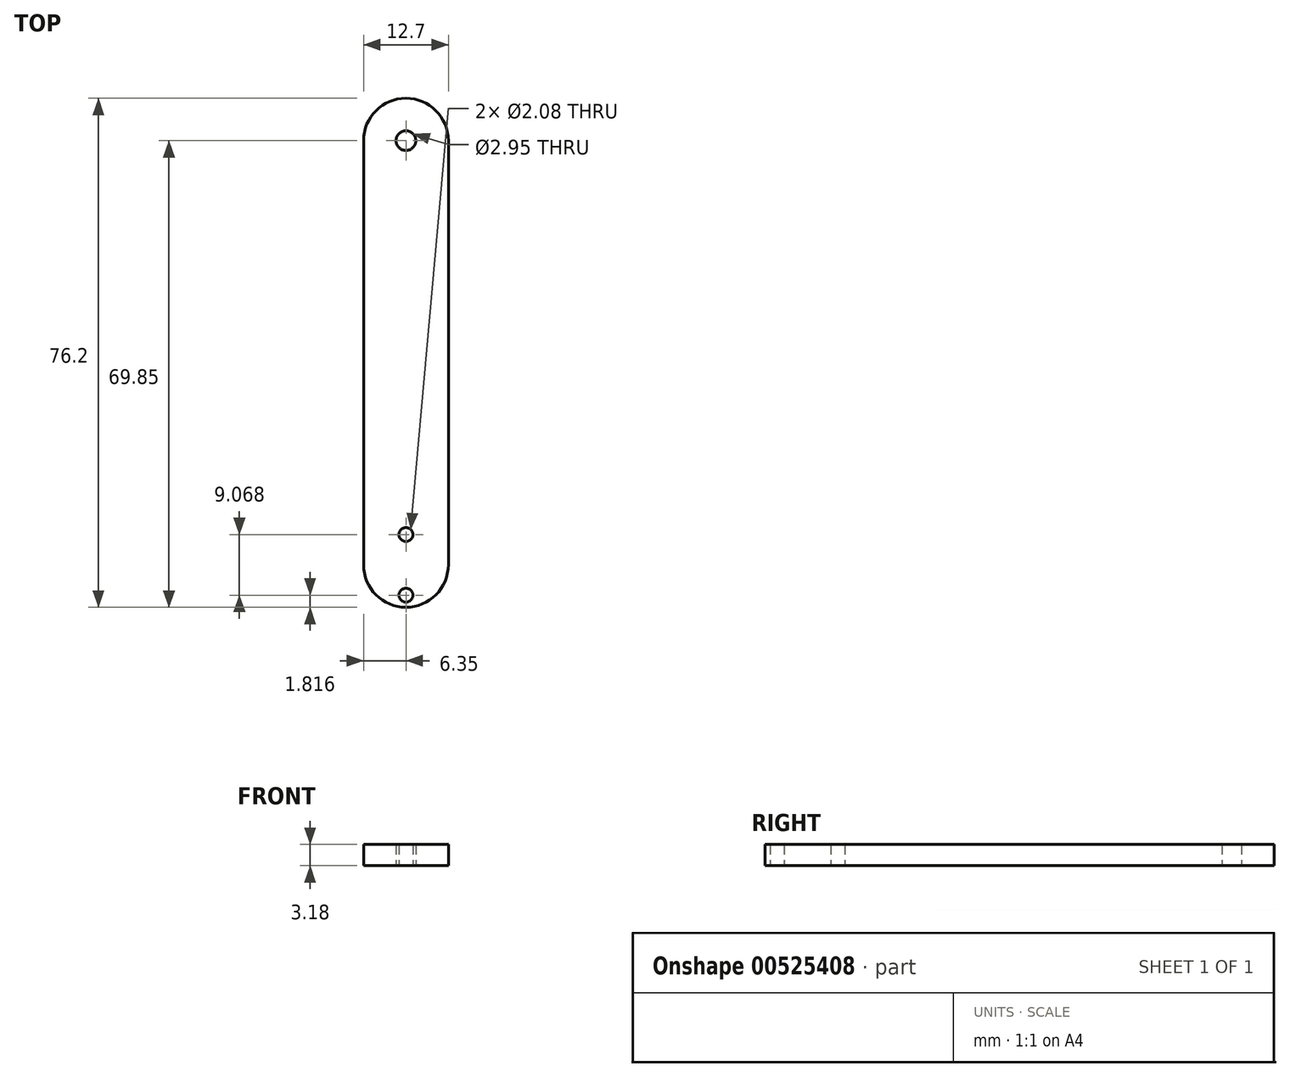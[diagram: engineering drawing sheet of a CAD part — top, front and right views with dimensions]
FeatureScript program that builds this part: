
annotation { "Feature Type Name" : "Feature", "Feature Type Description" : "" }
export const myFeature = defineFeature(function(context is Context, id is Id, definition is map)
    precondition{}
    {
        {
            var Q0;
            Q0=qCreatedBy(makeId("Top.planeOp"),FACE);
            var sketch = newSketch(context, id + "F0", { "sketchPlane" : qUnion([Q0])});
            skLineSegment(sketch, "E0.bottom", {"start": v(0, 38.1) * mm, "end": v(0, 38.1) * mm});
            skLineSegment(sketch, "E0.top", {"start": v(0, -38.1) * mm, "end": v(0, -38.1) * mm});
            skLineSegment(sketch, "E0.left", {"start": v(6.35, 31.75) * mm, "end": v(6.35, -31.75) * mm});
            skLineSegment(sketch, "E0.right", {"start": v(-6.35, 31.75) * mm, "end": v(-6.35, -31.75) * mm});
            skPoint(sketch, "E0.middle", {"position": v(0, 0) * mm});
            skCircle(sketch, "E1", {"center": v(0, -31.75) * mm, "radius": 1.47 * mm, "construction": true});
            skCircle(sketch, "E2.MirrorC", {"center": v(0, 31.75) * mm, "radius": 1.47 * mm});
            skPoint(sketch, "E3.visualSharp", {"position": v(6.35, 38.1) * mm});
            skArc(sketch, "E3.filletArc", {"start": v(6.35, 31.75) * mm, "mid": v(4.5, 36.24) * mm, "end": v(0, 38.1) * mm});
            skPoint(sketch, "E4.visualSharp", {"position": v(-6.35, 38.1) * mm});
            skArc(sketch, "E4.filletArc", {"start": v(0, 38.1) * mm, "mid": v(-4.5, 36.24) * mm, "end": v(-6.35, 31.75) * mm});
            skPoint(sketch, "E5.visualSharp", {"position": v(-6.35, -38.1) * mm});
            skArc(sketch, "E5.filletArc", {"start": v(-6.35, -31.75) * mm, "mid": v(-4.5, -36.24) * mm, "end": v(0, -38.1) * mm});
            skPoint(sketch, "E6.visualSharp", {"position": v(6.35, -38.1) * mm});
            skArc(sketch, "E6.filletArc", {"start": v(0, -38.1) * mm, "mid": v(4.5, -36.24) * mm, "end": v(6.35, -31.75) * mm});
            skCircle(sketch, "E7", {"center": v(0, -27.22) * mm, "radius": 1.04 * mm});
            skCircle(sketch, "E8", {"center": v(0, -36.28) * mm, "radius": 1.04 * mm});
            skLineSegment(sketch, "E9", {"start": v(0, -27.22) * mm, "end": v(0, -31.75) * mm, "construction": true});
            skLineSegment(sketch, "E10", {"start": v(0, -31.75) * mm, "end": v(0, -36.28) * mm, "construction": true});
            skSolve(sketch);
        }
        {
            var Q0;
            Q0=makeQuery(id+"F0.imprint","IMPRINT",FACE,{"disambiguationData":[TD([[makeQuery(id+"F0.imprint","IMPRINT",EDGE,{"derivedFrom":sQuery(id+"F0.wireOp",EDGE,"E0.left")}),-1.0]])]});
            extrude(context, id + "F1", {"entities" : qUnion([Q0]), "depth" : 3.17 * mm, "offsetDistance" : 25.4 * mm});
        }
    });
